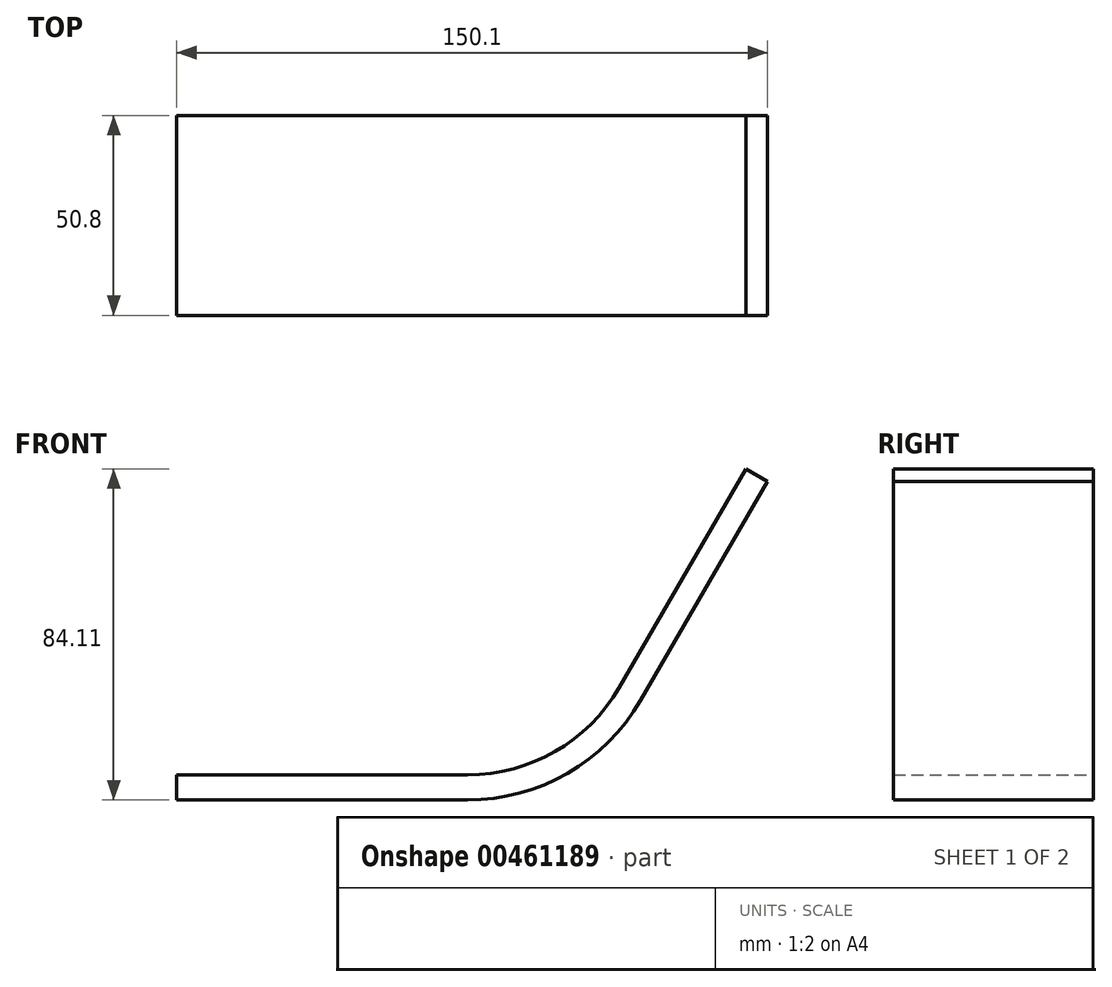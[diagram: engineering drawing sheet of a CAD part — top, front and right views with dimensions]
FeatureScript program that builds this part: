
annotation { "Feature Type Name" : "Feature", "Feature Type Description" : "" }
export const myFeature = defineFeature(function(context is Context, id is Id, definition is map)
    precondition{}
    {
        {
            var Q0;
            Q0=qCreatedBy(makeId("Front.planeOp"),FACE);
            var sketch = newSketch(context, id + "F0", { "sketchPlane" : qUnion([Q0])});
            skLineSegment(sketch, "E0", {"start": v(0, 0) * mm, "end": v(73.92, 0) * mm});
            skLineSegment(sketch, "E1", {"start": v(117.87, 25.32) * mm, "end": v(150.1, 80.92) * mm});
            skPoint(sketch, "E2.visualSharp", {"position": v(103.19, 0) * mm});
            skArc(sketch, "E2.filletArc", {"start": v(73.92, 0) * mm, "mid": v(99.28, 6.78) * mm, "end": v(117.87, 25.32) * mm});
            skLineSegment(sketch, "E3.0", {"start": v(112.37, 28.5) * mm, "end": v(144.6, 84.1) * mm});
            skArc(sketch, "E3.1", {"start": v(73.92, 6.35) * mm, "mid": v(96.1, 12.29) * mm, "end": v(112.37, 28.5) * mm});
            skLineSegment(sketch, "E3.2", {"start": v(0, 6.35) * mm, "end": v(73.92, 6.35) * mm});
            skLineSegment(sketch, "E4", {"start": v(0, 6.35) * mm, "end": v(0, 0) * mm});
            skLineSegment(sketch, "E5", {"start": v(144.6, 84.1) * mm, "end": v(150.1, 80.92) * mm});
            skSolve(sketch);
        }
        {
            var Q0;
            Q0 = qSketchRegion(id + "F0", true);
            extrude(context, id + "F1", {"entities" : qUnion([Q0]), "depth" : 50.8 * mm});
        }
    });
